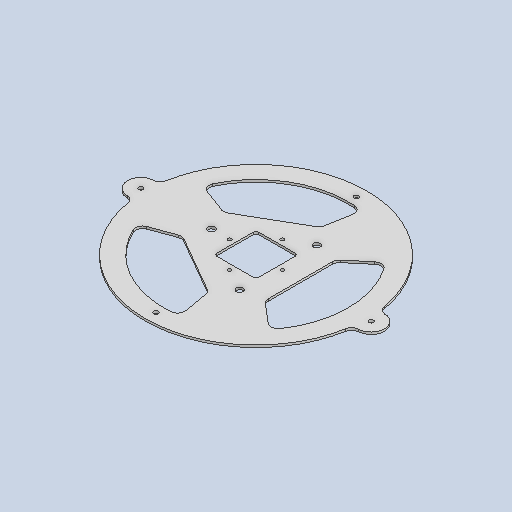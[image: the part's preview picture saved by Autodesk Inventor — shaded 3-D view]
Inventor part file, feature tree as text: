
AUTODESK INVENTOR PART (.ipt)
format: ipt  version: 2025.1 (Build 291241020, 241B)  size: 337,920 bytes
history: native  units: in
note: dims shown in document units (in); Inventor stores cm internally (conversion verified against a paired STEP export)
features: sketch x5, move_body x5, fillet x3, split x3, extrude x2, boolean_combine x1
ambient origin geometry x8: Origin, YZ Plane, XZ Plane, XY Plane, X Axis, Y Axis, Z Axis, Center Point
bodies: Solid25 (feature_tree)
feature tree (19):
  extrude  "Extrusion1"  Depth=2.3661in
  fillet  "Fillet1"  Radius=2.3661in
  extrude  "Extrusion2"  Depth=0.1575in
  fillet  "Fillet2"  Radius=0.1575in
  fillet  "Fillet3"  Radius=0.1575in
  sketch  "Sketch3"  dims[d9=0.201in d10=0.201in d11=2.9921in d12=1.4961in d13=2.9921in d14=1.4961in d15=0.375in d17=4.358in d20=0.375in d24=0.2525in d25=0.2525in d26=11.311in d27=5.6555in d30=1.5in d31=0.2525in d33=13.01in d34=0.125in d35=0.0in d36=0.4in d38=4.358in d39=4.358in d41=5.0322in d42=4.0in d43=2.0in d44=0.8933in d45=0.8933in d46=2.0in d47=2.0in d48=2.5in d49=0.0in d50=1.1811in d52=360.0deg d54=0.25in d55=0.0in d56=0.4in d57=0.4in d58=0.125in d59=1.1811in d61=360.0deg d63=0.125in d64=0.0in d65=2.0in d66=0.0in d67=1.0in d68=4.0in d69=1.0in d70=1.0in d71=0.0in d72=2.0in d73=2.0in d74=-4.0in d75=-1.0in d76=1.0in d77=-2.0in d78=0.0in]
  split  "Split5"
  split  "Split8"
  split  "Split9"
  boolean_combine  "Combine1"
  move_body  "Move Body1"
  move_body  "Move Body2"
  move_body  "Move Body3"
  move_body  "Move Body4"
  move_body  "Move Body5"
  sketch  "Sketch1"  dims[d0=12.5in d1=1.1831in d2=2.3661in]
  sketch  "Sketch2"  dims[d7=0.201in]
  sketch  "Sketch Circular Pattern1"  dims[d3=2.3661in d4=1.1831in d5=0.1575in d6=0.1575in]
  sketch  "Sketch Circular Pattern2"  dims[d8=0.201in]
